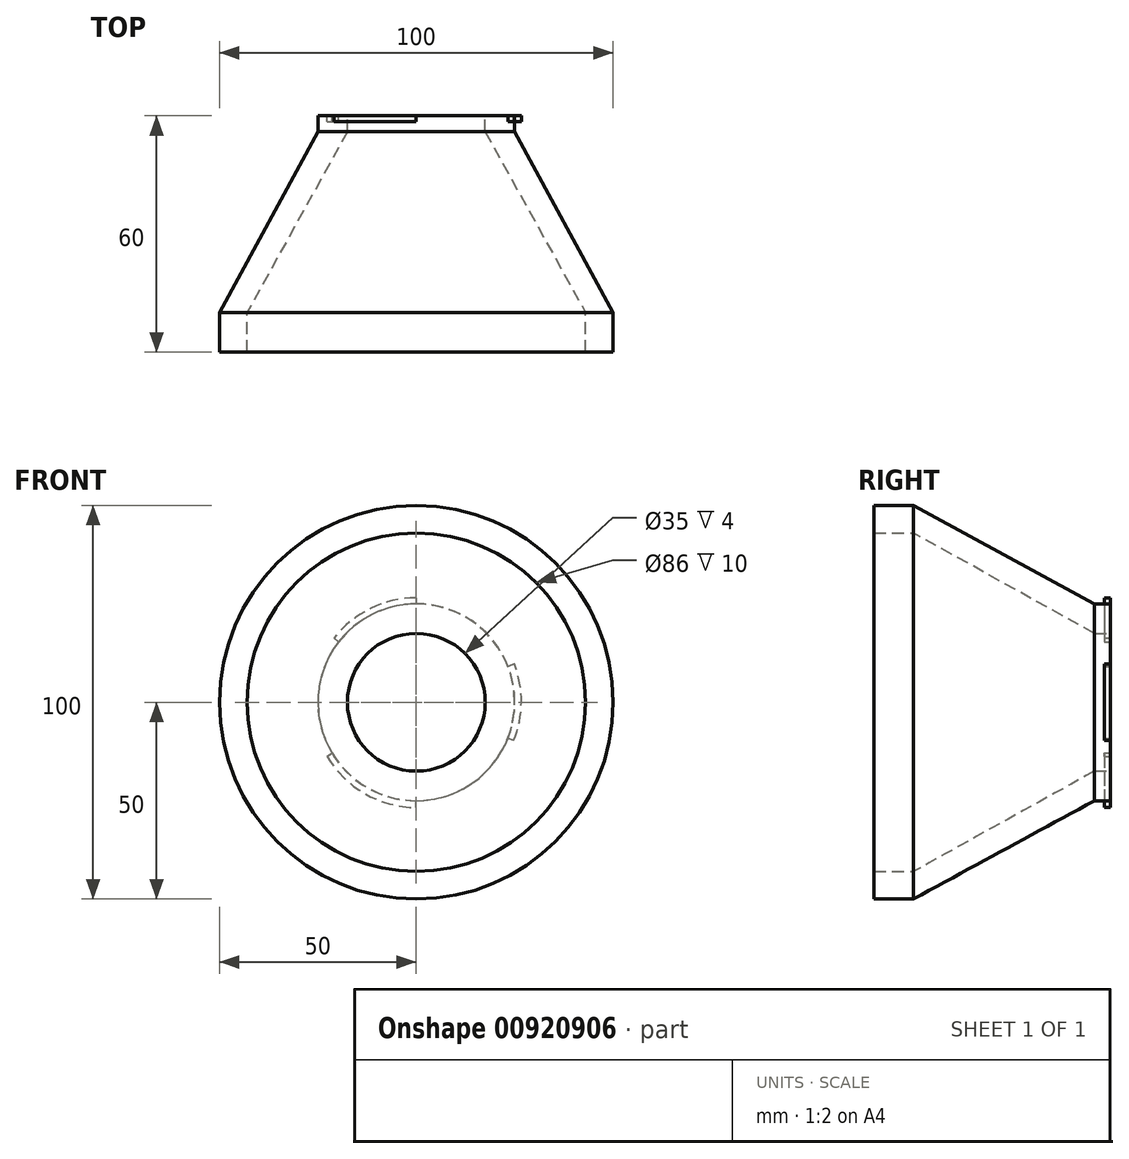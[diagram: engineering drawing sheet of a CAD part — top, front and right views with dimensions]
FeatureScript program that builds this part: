
annotation { "Feature Type Name" : "Feature", "Feature Type Description" : "" }
export const myFeature = defineFeature(function(context is Context, id is Id, definition is map)
    precondition{}
    {
        {
            var Q0;
            Q0=qCreatedBy(makeId("Front.planeOp"),FACE);
            var sketch = newSketch(context, id + "F0", { "sketchPlane" : qUnion([Q0])});
            skCircle(sketch, "E0", {"center": v(0, 0) * mm, "radius": 25 * mm});
            skArc(sketch, "E1", {"start": v(0, 26.5) * mm, "mid": v(-11.63, 23.81) * mm, "end": v(-20.9, 16.3) * mm});
            skArc(sketch, "E2", {"start": v(24.73, -9.74) * mm, "mid": v(26.69, 0) * mm, "end": v(24.91, 9.79) * mm});
            skArc(sketch, "E3", {"start": v(-22.68, -13.7) * mm, "mid": v(-13.06, -23.2) * mm, "end": v(0, -26.72) * mm});
            skLineSegment(sketch, "E4", {"start": v(-20.9, 16.3) * mm, "end": v(-19.71, 15.38) * mm});
            skLineSegment(sketch, "E5", {"start": v(0, 26.5) * mm, "end": v(0, 25) * mm});
            skLineSegment(sketch, "E6", {"start": v(24.91, 9.79) * mm, "end": v(23.27, 9.14) * mm});
            skLineSegment(sketch, "E7", {"start": v(24.73, -9.74) * mm, "end": v(23.26, -9.16) * mm});
            skLineSegment(sketch, "E8", {"start": v(0, -26.72) * mm, "end": v(0, -25) * mm});
            skLineSegment(sketch, "E9", {"start": v(-22.68, -13.7) * mm, "end": v(-21.4, -12.92) * mm});
            skCircle(sketch, "E10", {"center": v(0, 0) * mm, "radius": 17.5 * mm});
            skSolve(sketch);
        }
        {
            var Q0;
            Q0 = qSketchRegion(id + "F0", true);
            extrude(context, id + "F1", {"entities" : qUnion([Q0]), "depth" : 1.5 * mm, "offsetDistance" : 25 * mm});
        }
        {
            var Q0;
            Q0=makeQuery(id+"F1.opExtrude","CAP_FACE",FACE,{"disambiguationData":[OSD([sQuery(id+"F0.wireOp",EDGE,"E0"),sQuery(id+"F0.wireOp",EDGE,"E1"),sQuery(id+"F0.wireOp",EDGE,"E2"),sQuery(id+"F0.wireOp",EDGE,"E3"),sQuery(id+"F0.wireOp",EDGE,"E4"),sQuery(id+"F0.wireOp",EDGE,"E5"),sQuery(id+"F0.wireOp",EDGE,"E6"),sQuery(id+"F0.wireOp",EDGE,"E7"),sQuery(id+"F0.wireOp",EDGE,"E8"),sQuery(id+"F0.wireOp",EDGE,"E9"),sQuery(id+"F0.wireOp",EDGE,"rjy71EB8-ImHG-pkEu-g49G-hQzt3a2hd9ZZ")])],"isStart":false});
            var sketch = newSketch(context, id + "F2", { "sketchPlane" : qUnion([Q0])});
            skCircle(sketch, "E11", {"center": v(0, 0) * mm, "radius": 17.5 * mm});
            skCircle(sketch, "E12", {"center": v(0, 0) * mm, "radius": 25 * mm});
            skSolve(sketch);
        }
        {
            var Q0;
            Q0 = qSketchRegion(id + "F2", true);
            extrude(context, id + "F3", {"entities" : qUnion([Q0]), "operationType" : NewBodyOperationType.ADD, "depth" : 2.5 * mm, "offsetDistance" : 25 * mm});
        }
        {
            var Q0;
            Q0=qCreatedBy(makeId("Front.planeOp"),FACE);
            cPlane(context, id + "F4", {"entities" : qUnion([Q0]), "cplaneType" : CPlaneType.OFFSET, "offset" : 50 * mm, "width" : 150 * mm, "height" : 150 * mm});
        }
        {
            var Q0;
            Q0=makeQuery(id+"F3.opExtrude","CAP_FACE",FACE,{"disambiguationData":[OSD([sQuery(id+"F2.wireOp",EDGE,"E11"),sQuery(id+"F2.wireOp",EDGE,"E12")])],"isStart":false});
            var sketch = newSketch(context, id + "F5", { "sketchPlane" : qUnion([Q0])});
            skCircle(sketch, "E13", {"center": v(0, 0) * mm, "radius": 25 * mm});
            skSolve(sketch);
        }
        {
            var Q0;
            Q0=qCreatedBy(id+"F4.planeOp",FACE);
            var sketch = newSketch(context, id + "F6", { "sketchPlane" : qUnion([Q0])});
            skCircle(sketch, "E14", {"center": v(0, 0) * mm, "radius": 50 * mm});
            skSolve(sketch);
        }
        {
            var Q1;
            Q1 = qSketchRegion(id + "F6", true);
            var Q2;
            Q2 = qSketchRegion(id + "F5", true);
            loft(context, id + "F7", {"operationType" : NewBodyOperationType.ADD, "sheetProfilesArray" : [{ "sheetProfileEntities" : qUnion([Q1]) }, { "sheetProfileEntities" : qUnion([Q2]) }]});
        }
        {
            var Q0;
            Q0=makeQuery(id+"F7.opLoft","CAP_FACE",FACE,{"disambiguationData":[OSD([makeQuery(id+"F6.imprint","IMPRINT",FACE,{"disambiguationData":[TD([[makeQuery(id+"F6.imprint","IMPRINT",EDGE,{"derivedFrom":sQuery(id+"F6.wireOp",EDGE,"E14")}),1.0]])]})])],"isStart":true});
            var sketch = newSketch(context, id + "F8", { "sketchPlane" : qUnion([Q0])});
            skCircle(sketch, "E15", {"center": v(0, 0) * mm, "radius": 43 * mm});
            skSolve(sketch);
        }
        {
            var Q0;
            Q0=makeQuery(id+"F7.opLoft","CAP_FACE",FACE,{"disambiguationData":[OSD([makeQuery(id+"F5.imprint","IMPRINT",FACE,{"disambiguationData":[TD([[makeQuery(id+"F5.imprint","IMPRINT",EDGE,{"derivedFrom":makeQuery(id+"F3.opExtrude","CAP_EDGE",EDGE,{"disambiguationData":[OSD([sQuery(id+"F2.wireOp",EDGE,"E11")])],"isStart":false})}),1.0]])]})])],"isStart":true});
            var sketch = newSketch(context, id + "F9", { "sketchPlane" : qUnion([Q0])});
            skCircle(sketch, "E16", {"center": v(0, 0) * mm, "radius": 17.5 * mm});
            skSolve(sketch);
        }
        {
            var Q1;
            Q1 = qSketchRegion(id + "F9", true);
            var Q2;
            Q2 = qSketchRegion(id + "F8", true);
            loft(context, id + "F10", {"operationType" : NewBodyOperationType.REMOVE, "sheetProfilesArray" : [{ "sheetProfileEntities" : qUnion([Q1]) }, { "sheetProfileEntities" : qUnion([Q2]) }]});
        }
        {
            var Q0;
            Q0=makeQuery(id+"F7.opLoft","CAP_FACE",FACE,{"disambiguationData":[OSD([makeQuery(id+"F6.imprint","IMPRINT",FACE,{"disambiguationData":[TD([[makeQuery(id+"F6.imprint","IMPRINT",EDGE,{"derivedFrom":sQuery(id+"F6.wireOp",EDGE,"E14")}),1.0]])]})])],"isStart":true});
            var sketch = newSketch(context, id + "F11", { "sketchPlane" : qUnion([Q0])});
            skCircle(sketch, "E17", {"center": v(0, 0) * mm, "radius": 43 * mm});
            skCircle(sketch, "E18", {"center": v(0, 0) * mm, "radius": 50 * mm});
            skSolve(sketch);
        }
        {
            var Q0;
            Q0 = qSketchRegion(id + "F11", true);
            extrude(context, id + "F12", {"entities" : qUnion([Q0]), "operationType" : NewBodyOperationType.ADD, "depth" : 10 * mm, "offsetDistance" : 25 * mm});
        }
    });
